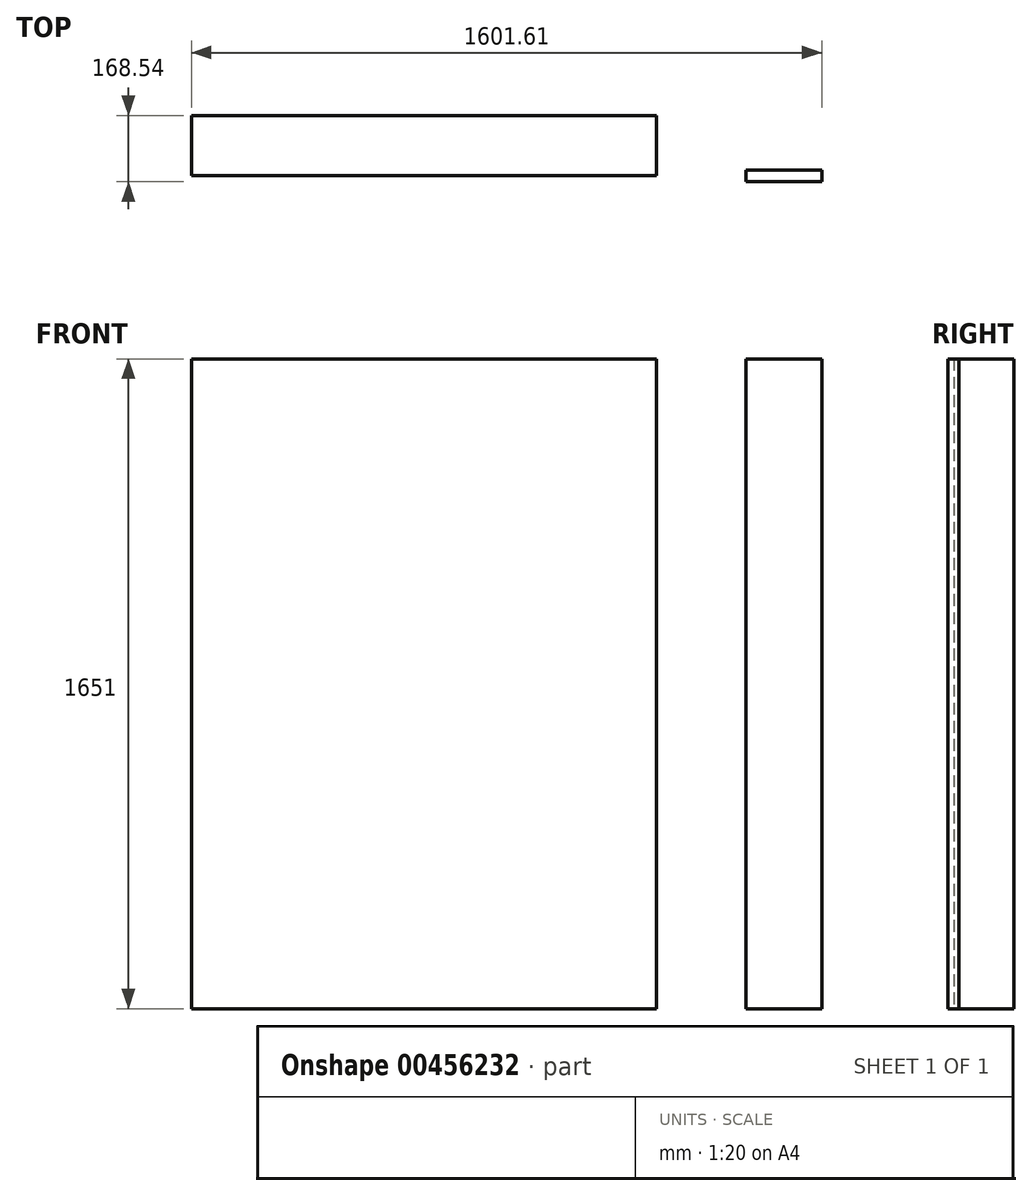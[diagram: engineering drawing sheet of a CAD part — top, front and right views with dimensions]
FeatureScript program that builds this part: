
annotation { "Feature Type Name" : "Feature", "Feature Type Description" : "" }
export const myFeature = defineFeature(function(context is Context, id is Id, definition is map)
    precondition{}
    {
        {
            var Q0;
            Q0=qCreatedBy(makeId("Top.planeOp"),FACE);
            var sketch = newSketch(context, id + "F0", { "sketchPlane" : qUnion([Q0])});
            skLineSegment(sketch, "E0.bottom", {"start": v(0, 0) * mm, "end": v(192.6, 0) * mm});
            skLineSegment(sketch, "E0.top", {"start": v(0, -28.95) * mm, "end": v(192.6, -28.95) * mm});
            skLineSegment(sketch, "E0.left", {"start": v(0, 0) * mm, "end": v(0, -28.95) * mm});
            skLineSegment(sketch, "E0.right", {"start": v(192.6, 0) * mm, "end": v(192.6, -28.95) * mm});
            skLineSegment(sketch, "E1.bottom", {"start": v(-227.25, -13.42) * mm, "end": v(-1409.02, -13.42) * mm});
            skLineSegment(sketch, "E1.top", {"start": v(-227.25, 139.59) * mm, "end": v(-1409.02, 139.59) * mm});
            skLineSegment(sketch, "E1.left", {"start": v(-227.25, -13.42) * mm, "end": v(-227.25, 139.59) * mm});
            skLineSegment(sketch, "E1.right", {"start": v(-1409.02, -13.42) * mm, "end": v(-1409.02, 139.59) * mm});
            skSolve(sketch);
        }
        {
            var Q0;
            Q0 = qSketchRegion(id + "F0", true);
            extrude(context, id + "F1", {"entities" : qUnion([Q0]), "depth" : 1651 * mm});
        }
    });
